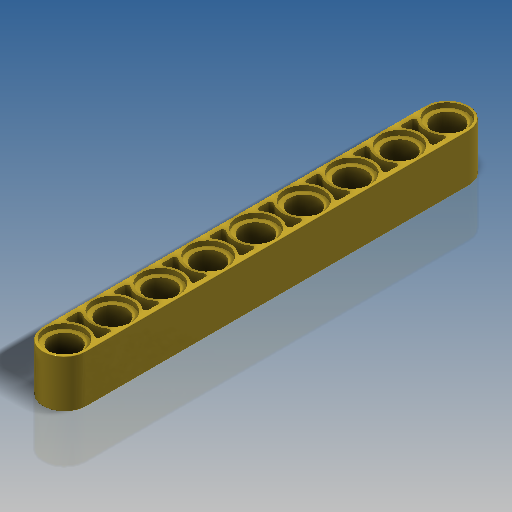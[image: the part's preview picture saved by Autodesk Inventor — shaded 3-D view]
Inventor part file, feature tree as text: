
AUTODESK INVENTOR PART (.ipt)
format: ipt  version: 2018.3 (Build 223284000, 284)  size: 467,456 bytes
history: native  units: mm
features: extrude x3, sketch x2, mirror x1, fillet x1
ambient origin geometry x8: Origin, YZ Plane, XZ Plane, XY Plane, X Axis, Y Axis, Z Axis, Center Point
bodies: Solid1 (feature_tree)
feature tree (7):
  extrude  "Extrusion1"  Depth=7.2mm
  sketch  "Sketch6"  dims[d41=0.8mm d42=0.0mm d43=3.1mm d44=0.0mm d48=64.0mm d49=6.4mm d50=4.8mm d52=0.8mm d53=80.0mm d55=8.0mm d56=10.0mm d58=10.0mm d60=0.4mm d61=0.1mm]
  extrude  "Extrusion7"  Depth=3.1mm TaperAngle=0.0deg
  extrude  "Extrusion8"  Depth=0.1mm
  mirror  "Mirror1"
  fillet  "Fillet2"  Radius=6.4mm
  sketch  "Sketch1"  dims[d14=8.0mm d15=0.0mm d32=7.2mm]
